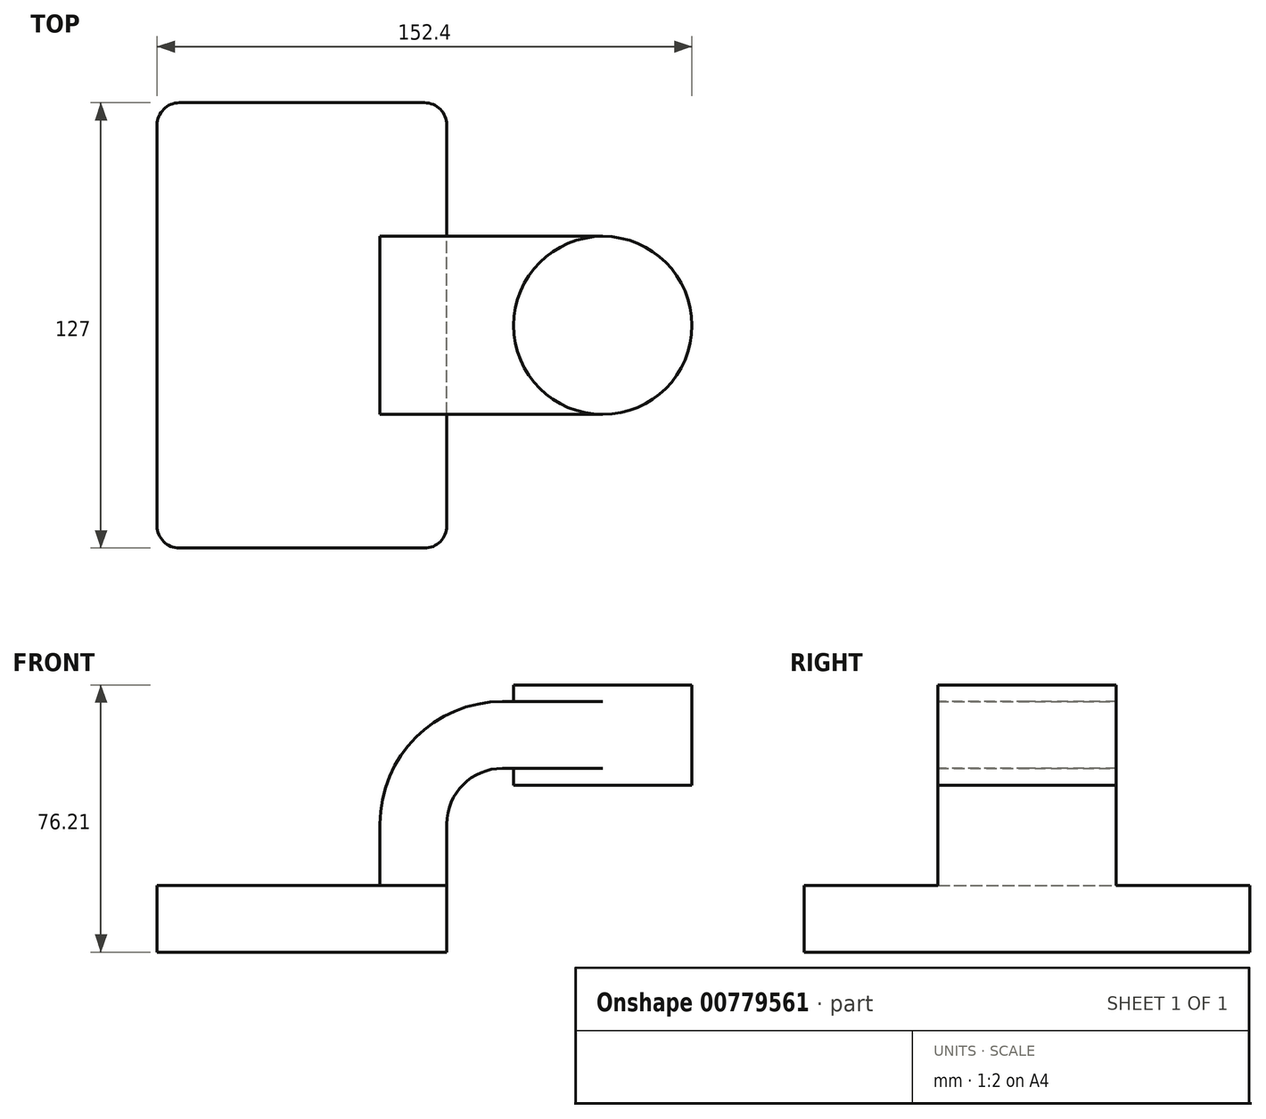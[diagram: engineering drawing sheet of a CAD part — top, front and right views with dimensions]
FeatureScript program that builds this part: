
annotation { "Feature Type Name" : "Feature", "Feature Type Description" : "" }
export const myFeature = defineFeature(function(context is Context, id is Id, definition is map)
    precondition{}
    {
        {
            var Q0;
            Q0=qCreatedBy(makeId("Front.planeOp"),FACE);
            var sketch = newSketch(context, id + "F0", { "sketchPlane" : qUnion([Q0])});
            skLineSegment(sketch, "E0.bottom", {"start": v(-41.28, 9.52) * mm, "end": v(41.27, 9.53) * mm});
            skLineSegment(sketch, "E0.top", {"start": v(-41.28, -9.53) * mm, "end": v(41.28, -9.53) * mm});
            skLineSegment(sketch, "E0.left", {"start": v(-41.28, 9.52) * mm, "end": v(-41.28, -9.53) * mm});
            skLineSegment(sketch, "E0.right", {"start": v(41.27, 9.53) * mm, "end": v(41.28, -9.52) * mm});
            skPoint(sketch, "E0.middle", {"position": v(0, 0) * mm});
            skLineSegment(sketch, "E1.bottom", {"start": v(60.32, 66.68) * mm, "end": v(111.12, 66.68) * mm});
            skLineSegment(sketch, "E1.top", {"start": v(60.32, 38.1) * mm, "end": v(111.12, 38.1) * mm});
            skLineSegment(sketch, "E1.left", {"start": v(60.32, 66.68) * mm, "end": v(60.32, 38.1) * mm});
            skLineSegment(sketch, "E1.right", {"start": v(111.12, 66.68) * mm, "end": v(111.12, 38.1) * mm});
            skPoint(sketch, "E1.middle", {"position": v(85.72, 52.39) * mm});
            skLineSegment(sketch, "E2", {"start": v(41.27, 9.53) * mm, "end": v(41.27, 27) * mm});
            skArc(sketch, "E3", {"start": v(41.27, 27) * mm, "mid": v(45.92, 38.23) * mm, "end": v(57.15, 42.88) * mm});
            skLineSegment(sketch, "E4", {"start": v(57.15, 42.88) * mm, "end": v(85.72, 42.88) * mm});
            skLineSegment(sketch, "E5.0", {"start": v(57.15, 61.93) * mm, "end": v(85.72, 61.93) * mm});
            skArc(sketch, "E5.1", {"start": v(22.22, 27) * mm, "mid": v(32.45, 51.7) * mm, "end": v(57.15, 61.93) * mm});
            skLineSegment(sketch, "E5.2", {"start": v(22.22, 9.53) * mm, "end": v(22.22, 27) * mm});
            skLineSegment(sketch, "E6", {"start": v(85.72, 38.1) * mm, "end": v(85.72, 66.68) * mm});
            skFitSpline(sketch, "E7", {"points": [v(-41.28, 9.52) * mm, v(57.15, 61.93) * mm], "startDerivative": vector(-0.11, 49.85) * mm, "endDerivative": vector(139.71, 0.07) * mm});
            skSolve(sketch);
        }
        {
            var Q0;
            Q0=makeQuery(id+"F0.imprint","IMPRINT",FACE,{"disambiguationData":[TD([[makeQuery(id+"F0.imprint","IMPRINT",EDGE,{"derivedFrom":sQuery(id+"F0.wireOp",EDGE,"E0.top")}),1.0]])]});
            extrude(context, id + "F1", {"entities" : qUnion([Q0]), "endBound" : BoundingType.SYMMETRIC, "depth" : 127 * mm, "offsetDistance" : 25.4 * mm});
        }
        {
            var Q0;
            {var subQ1=sQuery(id+"F0.wireOp",EDGE,"E2");Q0=makeQuery(id+"F0.imprint","IMPRINT",FACE,{"disambiguationData":[TD([[makeQuery(id+"F0.imprint","IMPRINT",EDGE,{"derivedFrom":subQ1}),1.0]])]});}
            var Q1;
            {var subQ0=sQuery(id+"F0.wireOp",EDGE,"E5.0");var subQ1=sQuery(id+"F0.wireOp",EDGE,"E1.left");var subQ2=makeQuery(id+"F0.imprint","INTERSECT",VERTEX,{"derivedFrom":[subQ1,subQ0]});Q1=makeQuery(id+"F0.imprint","IMPRINT",FACE,{"disambiguationData":[TD([[makeQuery(id+"F0.imprint","IMPRINT",EDGE,{"disambiguationData":[TD([[subQ2,-1.0]])],"derivedFrom":subQ1}),1.0]])]});}
            extrude(context, id + "F2", {"entities" : qUnion([Q0, Q1]), "operationType" : NewBodyOperationType.ADD, "endBound" : BoundingType.SYMMETRIC, "depth" : 50.8 * mm, "offsetDistance" : 25.4 * mm});
        }
        {
            var Q0;
            Q0=makeQuery(id+"F0.imprint","IMPRINT",FACE,{"disambiguationData":[TD([[makeQuery(id+"F0.imprint","IMPRINT",EDGE,{"derivedFrom":sQuery(id+"F0.wireOp",EDGE,"E5.1")}),1.0]])]});
            extrude(context, id + "F3", {"entities" : qUnion([Q0]), "operationType" : NewBodyOperationType.ADD, "endBound" : BoundingType.SYMMETRIC, "depth" : 15.88 * mm, "offsetDistance" : 25.4 * mm});
        }
        {
            var Q0;
            {var subQ0=sQuery(id+"F0.wireOp",EDGE,"E1.right");Q0=makeQuery(id+"F0.imprint","IMPRINT",FACE,{"disambiguationData":[TD([[makeQuery(id+"F0.imprint","IMPRINT",EDGE,{"derivedFrom":subQ0}),-1.0]])]});}
            var Q1;
            Q1=sQuery(id+"F0.wireOp",EDGE,"E6");
            revolve(context, id + "F4", {"operationType" : NewBodyOperationType.ADD, "surfaceOperationType" : NewSurfaceOperationType.NEW, "entities" : qUnion([Q0]), "axis" : qUnion([Q1]), "revolveType" : RevolveType.FULL});
        }
        {
            var Q0;
            Q0=makeQuery(id+"F1.opExtrude","CAP_EDGE",EDGE,{"disambiguationData":[OSD([sQuery(id+"F0.wireOp",EDGE,"E0.right")])],"isStart":false});
            var Q1;
            Q1=makeQuery(id+"F1.opExtrude","CAP_EDGE",EDGE,{"disambiguationData":[OSD([sQuery(id+"F0.wireOp",EDGE,"E0.left")])],"isStart":false});
            var Q2;
            Q2=makeQuery(id+"F1.opExtrude","CAP_EDGE",EDGE,{"disambiguationData":[OSD([sQuery(id+"F0.wireOp",EDGE,"E0.left")])],"isStart":true});
            var Q3;
            Q3=makeQuery(id+"F1.opExtrude","CAP_EDGE",EDGE,{"disambiguationData":[OSD([sQuery(id+"F0.wireOp",EDGE,"E0.right")])],"isStart":true});
            fillet(context, id + "F5", {"entities" : qUnion([Q0, Q1, Q2, Q3]), "radius" : 6.35 * mm, "tangentPropagation" : true, "allowEdgeOverflow" : false});
        }
    });
